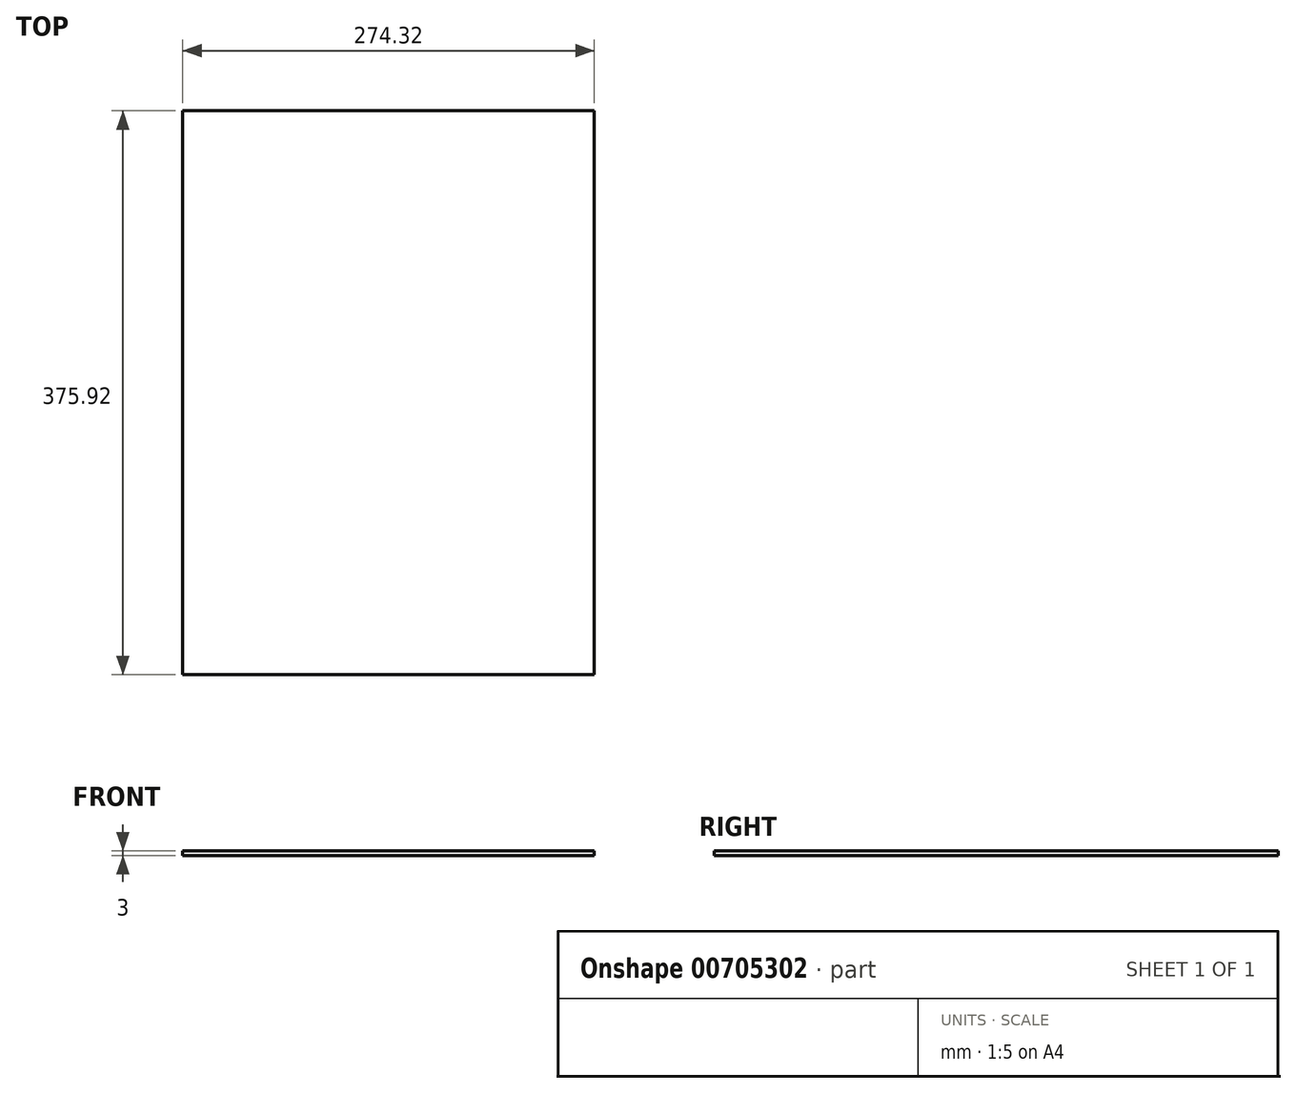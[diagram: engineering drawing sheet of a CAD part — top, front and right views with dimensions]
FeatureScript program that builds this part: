
annotation { "Feature Type Name" : "Feature", "Feature Type Description" : "" }
export const myFeature = defineFeature(function(context is Context, id is Id, definition is map)
    precondition{}
    {
        {
            var Q0;
            Q0=qCreatedBy(makeId("Top.planeOp"),FACE);
            var sketch = newSketch(context, id + "F0", { "sketchPlane" : qUnion([Q0])});
            skLineSegment(sketch, "E0.bottom", {"start": v(-137.16, 187.96) * mm, "end": v(137.16, 187.96) * mm});
            skLineSegment(sketch, "E0.top", {"start": v(-137.16, -187.96) * mm, "end": v(137.16, -187.96) * mm});
            skLineSegment(sketch, "E0.left", {"start": v(-137.16, 187.96) * mm, "end": v(-137.16, -187.96) * mm});
            skLineSegment(sketch, "E0.right", {"start": v(137.16, 187.96) * mm, "end": v(137.16, -187.96) * mm});
            skPoint(sketch, "E0.middle", {"position": v(0, 0) * mm});
            skSolve(sketch);
        }
        {
            var Q0;
            Q0 = qSketchRegion(id + "F0", true);
            extrude(context, id + "F1", {"entities" : qUnion([Q0]), "depth" : 3 * mm, "offsetDistance" : 25.4 * mm});
        }
    });
